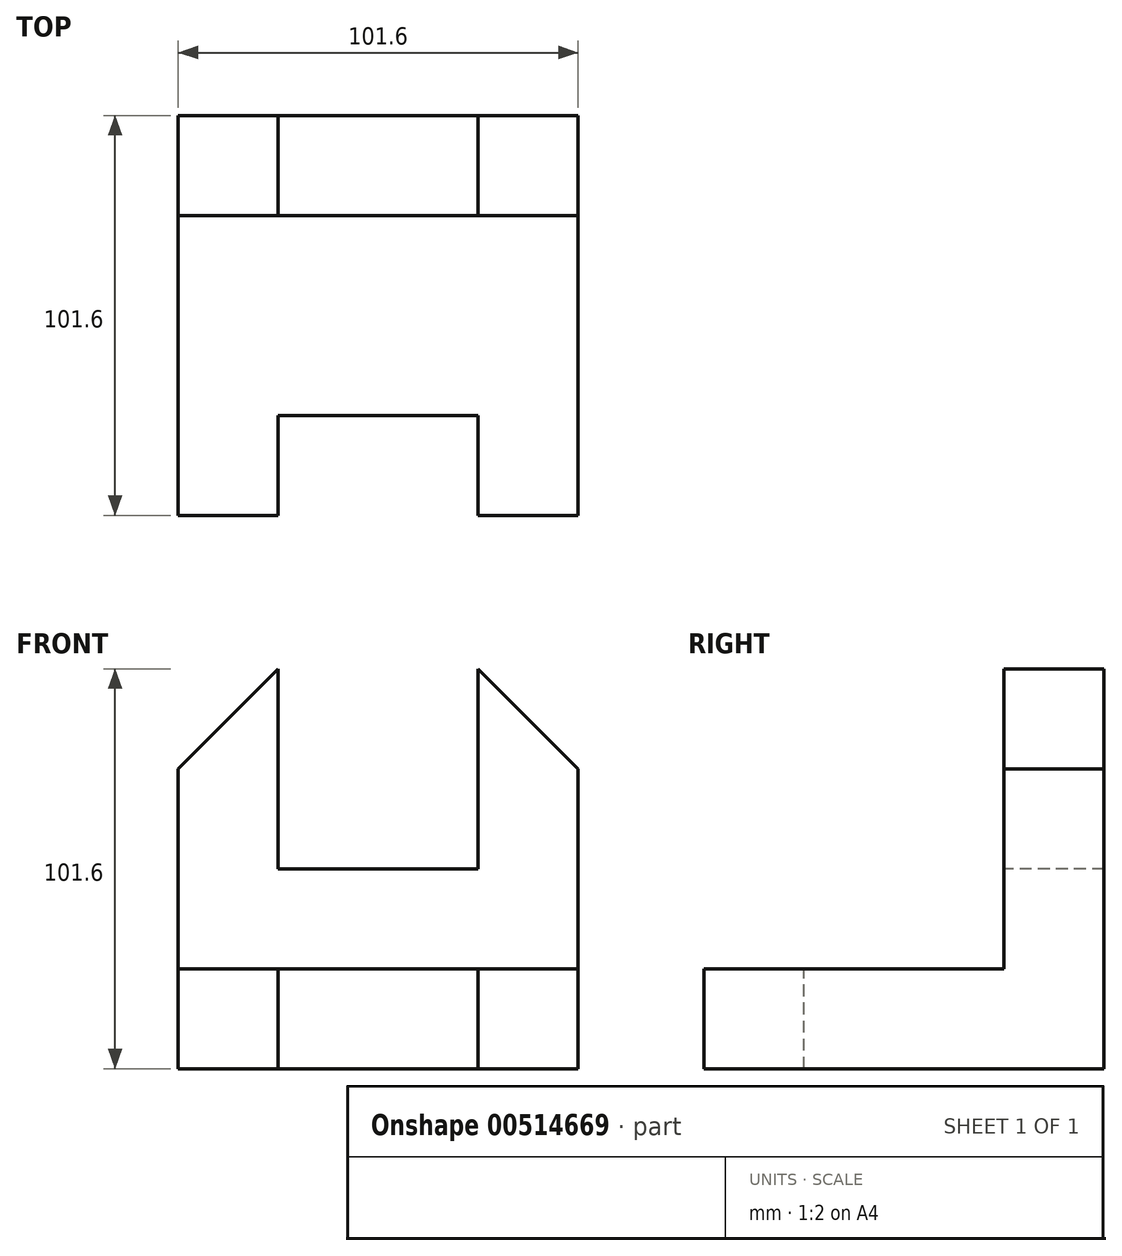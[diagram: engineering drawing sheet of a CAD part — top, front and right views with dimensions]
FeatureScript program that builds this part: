
annotation { "Feature Type Name" : "Feature", "Feature Type Description" : "" }
export const myFeature = defineFeature(function(context is Context, id is Id, definition is map)
    precondition{}
    {
        {
            var Q0;
            Q0=qCreatedBy(makeId("Front.planeOp"),FACE);
            var sketch = newSketch(context, id + "F0", { "sketchPlane" : qUnion([Q0])});
            skLineSegment(sketch, "E0", {"start": v(0, 0) * mm, "end": v(0, 101.6) * mm});
            skLineSegment(sketch, "E1", {"start": v(0, 101.6) * mm, "end": v(101.6, 101.6) * mm});
            skLineSegment(sketch, "E2", {"start": v(101.6, 101.6) * mm, "end": v(101.6, 0) * mm});
            skLineSegment(sketch, "E3", {"start": v(101.6, 0) * mm, "end": v(0, 0) * mm});
            skSolve(sketch);
        }
        {
            var Q0;
            Q0=makeQuery(id+"F0.imprint","IMPRINT",FACE,{"disambiguationData":[TD([[makeQuery(id+"F0.imprint","IMPRINT",EDGE,{"derivedFrom":sQuery(id+"F0.wireOp",EDGE,"E0")}),-1.0]])]});
            extrude(context, id + "F1", {"entities" : qUnion([Q0]), "oppositeDirection" : true, "depth" : 101.6 * mm, "offsetDistance" : 25.4 * mm});
        }
        {
            var Q0;
            Q0=makeQuery(id+"F1.opExtrude","SWEPT_FACE",FACE,{"disambiguationData":[OSD([sQuery(id+"F0.wireOp",EDGE,"E2")])]});
            var sketch = newSketch(context, id + "F2", { "sketchPlane" : qUnion([Q0])});
            skLineSegment(sketch, "E4", {"start": v(0, 0) * mm, "end": v(0, 25.4) * mm});
            skLineSegment(sketch, "E5", {"start": v(0, 25.4) * mm, "end": v(76.2, 25.4) * mm});
            skLineSegment(sketch, "E6", {"start": v(76.2, 25.4) * mm, "end": v(76.2, 101.6) * mm});
            skSolve(sketch);
        }
        {
            var Q0;
            {var subQ0=sQuery(id+"F2.wireOp",EDGE,"E5");Q0=makeQuery(id+"F2.imprint","IMPRINT",FACE,{"disambiguationData":[TD([[makeQuery(id+"F2.imprint","IMPRINT",EDGE,{"derivedFrom":subQ0}),1.0]])]});}
            extrude(context, id + "F3", {"entities" : qUnion([Q0]), "operationType" : NewBodyOperationType.REMOVE, "oppositeDirection" : true, "depth" : 101.6 * mm, "offsetDistance" : 25.4 * mm});
        }
        {
            var Q0;
            Q0=makeQuery(id+"F1.opExtrude","CAP_FACE",FACE,{"disambiguationData":[OSD([sQuery(id+"F0.wireOp",EDGE,"E0"),sQuery(id+"F0.wireOp",EDGE,"E1"),sQuery(id+"F0.wireOp",EDGE,"E2"),sQuery(id+"F0.wireOp",EDGE,"E3")])],"isStart":true});
            var sketch = newSketch(context, id + "F4", { "sketchPlane" : qUnion([Q0])});
            skLineSegment(sketch, "E7", {"start": v(0, 0) * mm, "end": v(25.4, 0) * mm});
            skLineSegment(sketch, "E8", {"start": v(25.4, 0) * mm, "end": v(25.4, 25.4) * mm});
            skLineSegment(sketch, "E9", {"start": v(25.4, 25.4) * mm, "end": v(76.2, 25.4) * mm});
            skLineSegment(sketch, "E10", {"start": v(76.2, 25.4) * mm, "end": v(76.2, 0) * mm});
            skSolve(sketch);
        }
        {
            var Q0;
            {var subQ0=sQuery(id+"F4.wireOp",EDGE,"E8");Q0=makeQuery(id+"F4.imprint","IMPRINT",FACE,{"disambiguationData":[TD([[makeQuery(id+"F4.imprint","IMPRINT",EDGE,{"derivedFrom":subQ0}),-1.0]])]});}
            extrude(context, id + "F5", {"entities" : qUnion([Q0]), "operationType" : NewBodyOperationType.REMOVE, "oppositeDirection" : true, "depth" : 25.4 * mm, "offsetDistance" : 25.4 * mm});
        }
        {
            var Q0;
            Q0=makeQuery(id+"F3.boolean.opBoolean","COPY",FACE,{"derivedFrom":makeQuery(id+"F3.opExtrude","SWEPT_FACE",FACE,{"disambiguationData":[OSD([sQuery(id+"F2.wireOp",EDGE,"E6")])]})});
            var sketch = newSketch(context, id + "F6", { "sketchPlane" : qUnion([Q0])});
            skLineSegment(sketch, "E11", {"start": v(0, 101.6) * mm, "end": v(25.4, 101.6) * mm});
            skLineSegment(sketch, "E12", {"start": v(25.4, 101.6) * mm, "end": v(25.4, 50.8) * mm});
            skLineSegment(sketch, "E13", {"start": v(25.4, 50.8) * mm, "end": v(76.2, 50.8) * mm});
            skLineSegment(sketch, "E14", {"start": v(76.2, 50.8) * mm, "end": v(76.2, 101.6) * mm});
            skSolve(sketch);
        }
        {
            var Q0;
            Q0 = qSketchRegion(id + "F6", true);
            var Q1;
            {var subQ0=sQuery(id+"F6.wireOp",EDGE,"E12");Q1=makeQuery(id+"F6.imprint","IMPRINT",FACE,{"disambiguationData":[TD([[makeQuery(id+"F6.imprint","IMPRINT",EDGE,{"derivedFrom":subQ0}),1.0]])]});}
            extrude(context, id + "F7", {"entities" : qUnion([Q0, Q1]), "operationType" : NewBodyOperationType.REMOVE, "oppositeDirection" : true, "depth" : 25.4 * mm, "offsetDistance" : 25.4 * mm});
        }
        {
            var Q0;
            Q0=makeQuery(id+"F3.boolean.opBoolean","COPY",FACE,{"derivedFrom":makeQuery(id+"F3.opExtrude","SWEPT_FACE",FACE,{"disambiguationData":[OSD([sQuery(id+"F2.wireOp",EDGE,"E6")])]})});
            var sketch = newSketch(context, id + "F8", { "sketchPlane" : qUnion([Q0])});
            skLineSegment(sketch, "E15", {"start": v(25.4, 101.6) * mm, "end": v(25.4, 76.2) * mm});
            skLineSegment(sketch, "E16", {"start": v(25.4, 76.2) * mm, "end": v(0, 76.2) * mm});
            skLineSegment(sketch, "E17", {"start": v(0, 76.2) * mm, "end": v(25.4, 101.6) * mm});
            skLineSegment(sketch, "E18", {"start": v(76.2, 101.6) * mm, "end": v(76.2, 76.2) * mm});
            skLineSegment(sketch, "E19", {"start": v(76.2, 76.2) * mm, "end": v(101.6, 76.2) * mm});
            skLineSegment(sketch, "E20", {"start": v(101.6, 76.2) * mm, "end": v(76.2, 101.6) * mm});
            skSolve(sketch);
        }
        {
            var Q0;
            {var subQ0=sQuery(id+"F8.wireOp",EDGE,"E17");Q0=makeQuery(id+"F8.imprint","IMPRINT",FACE,{"disambiguationData":[TD([[makeQuery(id+"F8.imprint","IMPRINT",EDGE,{"derivedFrom":subQ0}),1.0]])]});}
            extrude(context, id + "F9", {"entities" : qUnion([Q0]), "operationType" : NewBodyOperationType.REMOVE, "oppositeDirection" : true, "depth" : 25.4 * mm, "offsetDistance" : 25.4 * mm});
        }
        {
            var Q0;
            Q0=makeQuery(id+"F3.boolean.opBoolean","COPY",FACE,{"derivedFrom":makeQuery(id+"F3.opExtrude","SWEPT_FACE",FACE,{"disambiguationData":[OSD([sQuery(id+"F2.wireOp",EDGE,"E6")])]})});
            var sketch = newSketch(context, id + "F10", { "sketchPlane" : qUnion([Q0])});
            skLineSegment(sketch, "E21", {"start": v(76.2, 101.6) * mm, "end": v(76.2, 76.2) * mm});
            skLineSegment(sketch, "E22", {"start": v(76.2, 76.2) * mm, "end": v(101.6, 76.2) * mm});
            skLineSegment(sketch, "E23", {"start": v(101.6, 76.2) * mm, "end": v(76.2, 101.6) * mm});
            skSolve(sketch);
        }
        {
            var Q0;
            {var subQ0=sQuery(id+"F10.wireOp",EDGE,"E23");Q0=makeQuery(id+"F10.imprint","IMPRINT",FACE,{"disambiguationData":[TD([[makeQuery(id+"F10.imprint","IMPRINT",EDGE,{"derivedFrom":subQ0}),-1.0]])]});}
            extrude(context, id + "F11", {"entities" : qUnion([Q0]), "operationType" : NewBodyOperationType.REMOVE, "oppositeDirection" : true, "depth" : 25.4 * mm, "offsetDistance" : 25.4 * mm});
        }
    });
